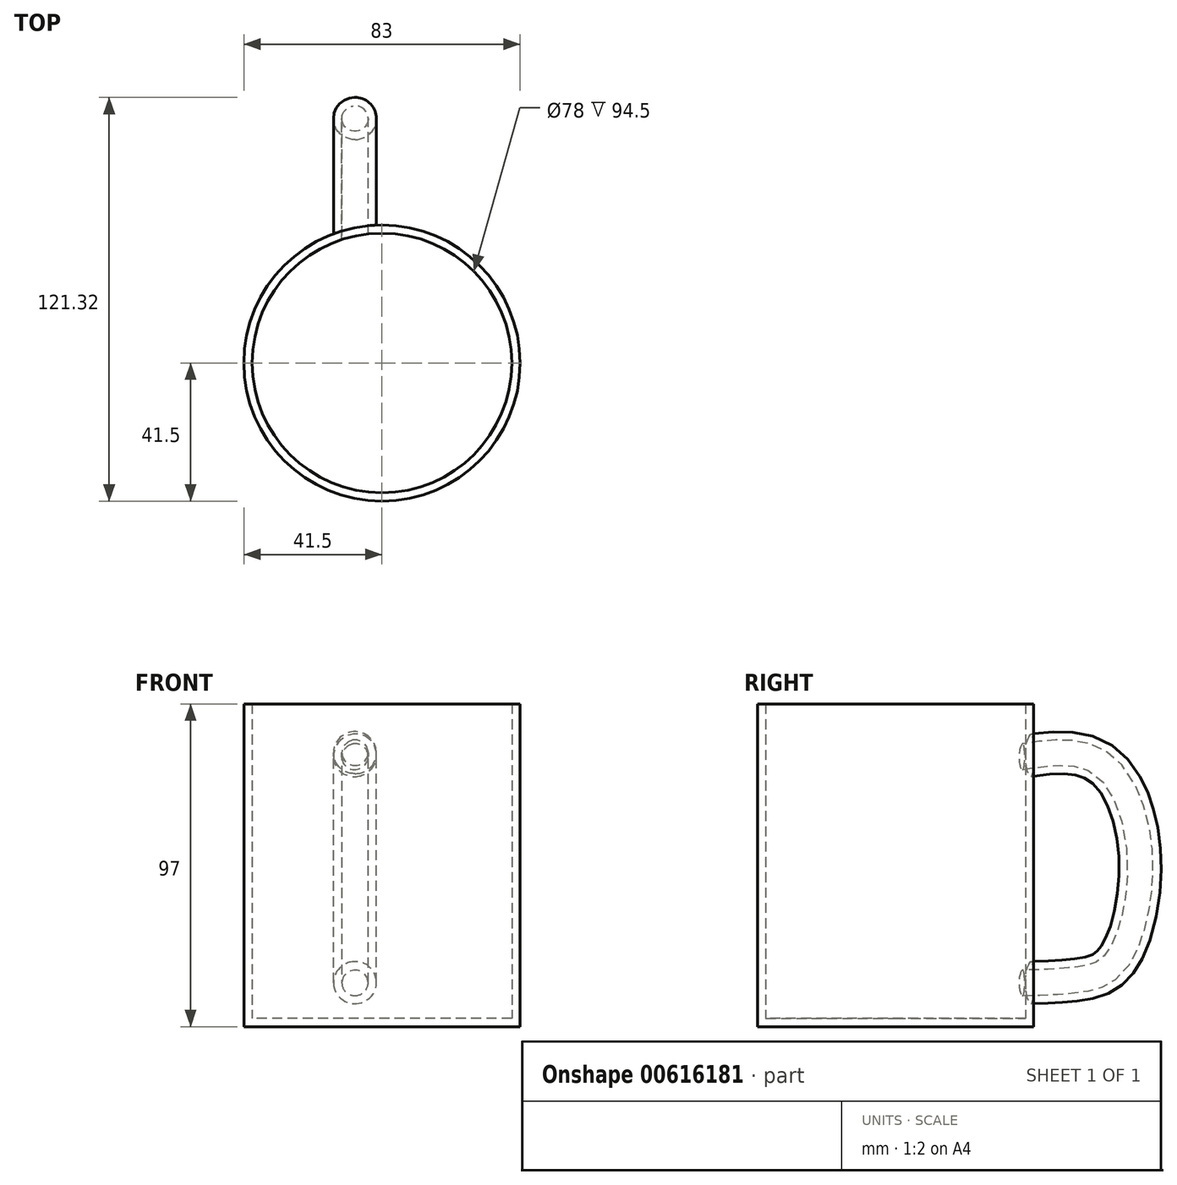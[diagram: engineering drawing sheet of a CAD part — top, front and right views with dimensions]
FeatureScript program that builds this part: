
annotation { "Feature Type Name" : "Feature", "Feature Type Description" : "" }
export const myFeature = defineFeature(function(context is Context, id is Id, definition is map)
    precondition{}
    {
        {
            var Q0;
            Q0=qCreatedBy(makeId("Top.planeOp"),FACE);
            var sketch = newSketch(context, id + "F0", { "sketchPlane" : qUnion([Q0])});
            skCircle(sketch, "E0", {"center": v(0, 0) * mm, "radius": 41.5 * mm});
            skSolve(sketch);
        }
        {
            var Q0;
            Q0=makeQuery(id+"F0.imprint","IMPRINT",FACE,{"disambiguationData":[TD([[makeQuery(id+"F0.imprint","IMPRINT",EDGE,{"derivedFrom":sQuery(id+"F0.wireOp",EDGE,"E0")}),1.0]])]});
            extrude(context, id + "F1", {"entities" : qUnion([Q0]), "depth" : 97 * mm, "offsetDistance" : 25 * mm});
        }
        {
            var Q0;
            Q0=qCreatedBy(makeId("Right.planeOp"),FACE);
            var sketch = newSketch(context, id + "F2", { "sketchPlane" : qUnion([Q0])});
            skFitSpline(sketch, "E1", {"points": [v(31.03, 79.82) * mm, v(60.73, 79.82) * mm, v(73.46, 51.18) * mm, v(66.03, 19.36) * mm, v(54.36, 14.05) * mm, v(33.15, 13) * mm], "startDerivative": vector(151.57, 30.81) * mm, "endDerivative": vector(-122.88, -2.5) * mm});
            skSolve(sketch);
        }
        {
            var Q0;
            Q0=qCreatedBy(makeId("Front.planeOp"),FACE);
            cPlane(context, id + "F3", {"entities" : qUnion([Q0]), "cplaneType" : CPlaneType.OFFSET, "offset" : 34 * mm, "oppositeDirection" : true, "width" : 150 * mm, "height" : 150 * mm});
        }
        {
            var Q0;
            Q0=qCreatedBy(id+"F3.planeOp",FACE);
            var sketch = newSketch(context, id + "F4", { "sketchPlane" : qUnion([Q0])});
            skCircle(sketch, "E2", {"center": v(-8.1, 80.36) * mm, "radius": 6.45 * mm});
            skSolve(sketch);
        }
        {
            var Q0;
            Q0 = qSketchRegion(id + "F4", true);
            var Q1;
            Q1=sQuery(id+"F2.wireOp",EDGE,"E1");
            sweep(context, id + "F5", {"operationType" : NewBodyOperationType.ADD, "profiles" : qUnion([Q0]), "path" : qUnion([Q1])});
        }
        {
            var Q0;
            Q0=makeQuery(id+"F1.opExtrude","CAP_FACE",FACE,{"disambiguationData":[OSD([sQuery(id+"F0.wireOp",EDGE,"E0")])],"isStart":false});
            shell(context, id + "F6", {"entities" : qUnion([Q0]), "thickness" : 2.5 * mm});
        }
    });
